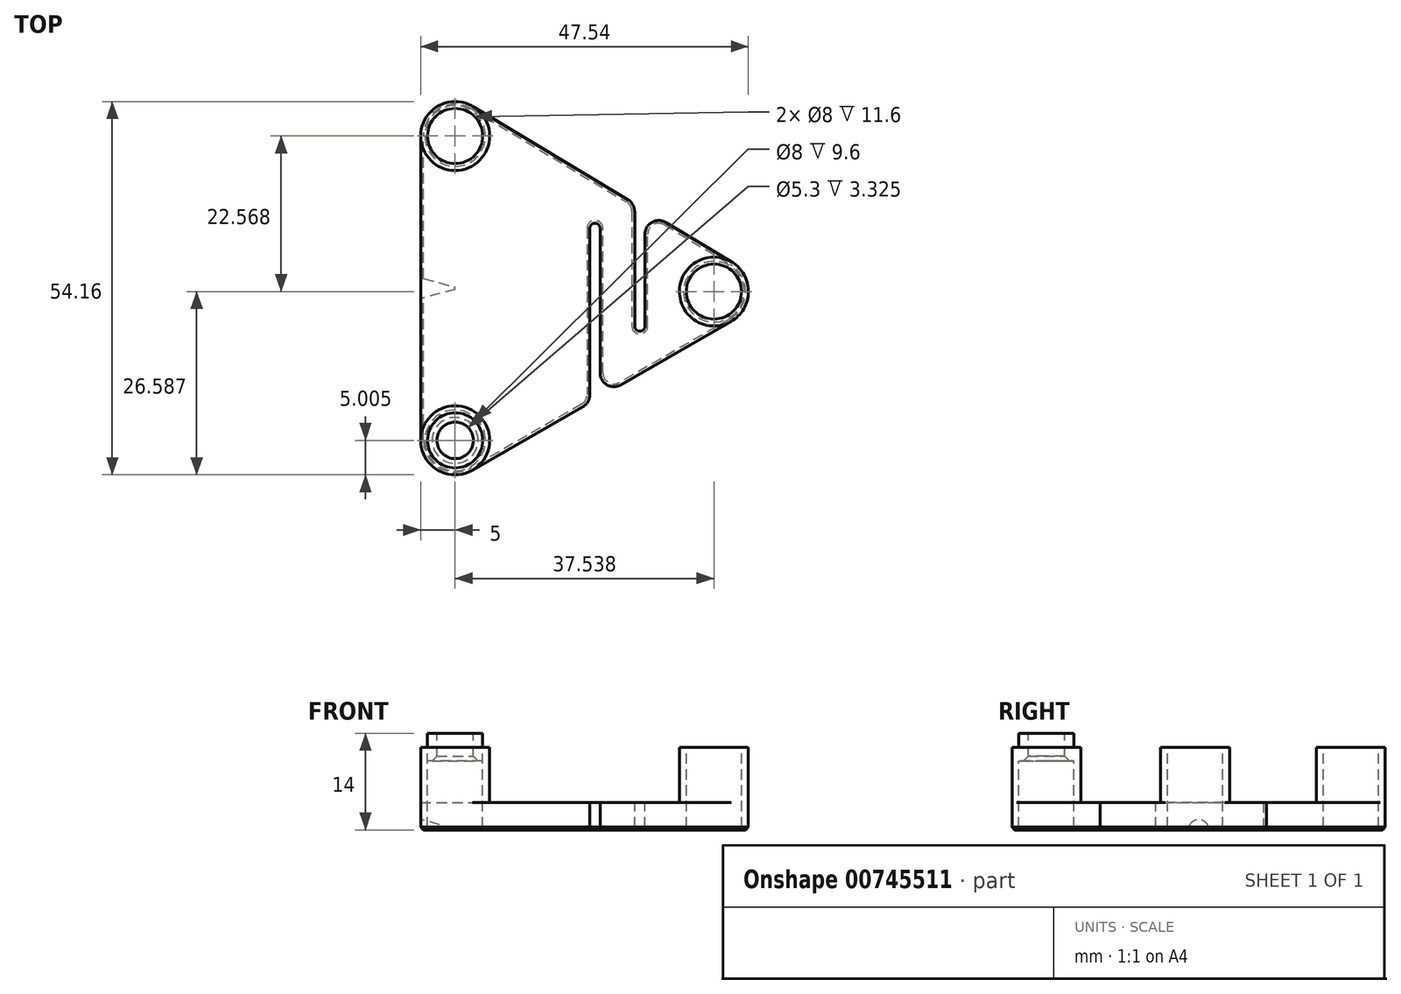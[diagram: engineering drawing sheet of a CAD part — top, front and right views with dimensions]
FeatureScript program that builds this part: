
annotation { "Feature Type Name" : "Feature", "Feature Type Description" : "" }
export const myFeature = defineFeature(function(context is Context, id is Id, definition is map)
    precondition{}
    {
        {
            var Q0;
            Q0=qCreatedBy(makeId("Top.planeOp"),FACE);
            var sketch = newSketch(context, id + "F0", { "sketchPlane" : qUnion([Q0])});
            skLineSegment(sketch, "E0", {"start": v(-11.93, 22.08) * mm, "end": v(25.6, 0.5) * mm, "construction": true});
            skLineSegment(sketch, "E1", {"start": v(25.6, 0.5) * mm, "end": v(-11.93, -22.07) * mm, "construction": true});
            skLineSegment(sketch, "E2", {"start": v(-11.93, -22.07) * mm, "end": v(-11.93, 22.07) * mm, "construction": true});
            skLineSegment(sketch, "E3", {"start": v(0, 0) * mm, "end": v(-11.93, 0) * mm, "construction": true});
            skCircle(sketch, "E4", {"center": v(-11.93, 22.07) * mm, "radius": 2.65 * mm});
            skCircle(sketch, "E5", {"center": v(-11.93, -22.07) * mm, "radius": 2.65 * mm});
            skCircle(sketch, "E6", {"center": v(25.6, 0.5) * mm, "radius": 2.65 * mm});
            skCircle(sketch, "E7", {"center": v(-11.93, 22.07) * mm, "radius": 4 * mm});
            skCircle(sketch, "E8", {"center": v(-11.93, -22.07) * mm, "radius": 4 * mm});
            skCircle(sketch, "E9", {"center": v(25.6, 0.5) * mm, "radius": 4 * mm});
            skLineSegment(sketch, "E10.0", {"start": v(-16.93, -30.92) * mm, "end": v(-16.93, 30.72) * mm});
            skLineSegment(sketch, "E10.1", {"start": v(35.47, 0.59) * mm, "end": v(-16.93, -30.92) * mm});
            skLineSegment(sketch, "E10.2", {"start": v(-16.93, 30.72) * mm, "end": v(35.47, 0.59) * mm});
            skLineSegment(sketch, "E11.top", {"start": v(7.6, -9.43) * mm, "end": v(9.1, -9.43) * mm});
            skLineSegment(sketch, "E11.left", {"start": v(7.6, 16.6) * mm, "end": v(7.6, -9.43) * mm});
            skLineSegment(sketch, "E11.right", {"start": v(9.1, 15.75) * mm, "end": v(9.1, -9.43) * mm});
            skLineSegment(sketch, "E12.bottom", {"start": v(14.1, 6.24) * mm, "end": v(15.6, 6.24) * mm});
            skLineSegment(sketch, "E12.left", {"start": v(14.1, 6.24) * mm, "end": v(14.1, -12.25) * mm});
            skLineSegment(sketch, "E12.right", {"start": v(15.6, 6.24) * mm, "end": v(15.6, -11.35) * mm});
            skCircle(sketch, "E13", {"center": v(-11.93, 22.07) * mm, "radius": 5 * mm});
            skCircle(sketch, "E14", {"center": v(-11.93, -22.07) * mm, "radius": 5 * mm});
            skCircle(sketch, "E15", {"center": v(25.6, 0.5) * mm, "radius": 5 * mm});
            skSolve(sketch);
        }
        {
            var Q0;
            Q0=makeQuery(id+"F0.imprint","IMPRINT",FACE,{"disambiguationData":[TD([[makeQuery(id+"F0.imprint","IMPRINT",EDGE,{"derivedFrom":sQuery(id+"F0.wireOp",EDGE,"E11.top")}),-1.0]])]});
            var Q1;
            Q1=makeQuery(id+"F0.imprint","IMPRINT",FACE,{"disambiguationData":[TD([[makeQuery(id+"F0.imprint","IMPRINT",EDGE,{"derivedFrom":sQuery(id+"F0.wireOp",EDGE,"E7")}),-1.0]])]});
            var Q2;
            Q2=makeQuery(id+"F0.imprint","IMPRINT",FACE,{"disambiguationData":[TD([[makeQuery(id+"F0.imprint","IMPRINT",EDGE,{"derivedFrom":sQuery(id+"F0.wireOp",EDGE,"E8")}),-1.0]])]});
            var Q3;
            Q3=makeQuery(id+"F0.imprint","IMPRINT",FACE,{"disambiguationData":[TD([[makeQuery(id+"F0.imprint","IMPRINT",EDGE,{"derivedFrom":sQuery(id+"F0.wireOp",EDGE,"E9")}),-1.0]])]});
            extrude(context, id + "F1", {"entities" : qUnion([Q0, Q1, Q2, Q3]), "depth" : 4 * mm, "offsetDistance" : 25 * mm});
        }
        {
            var Q0;
            Q0=makeQuery(id+"F1.opExtrude","SWEPT_EDGE",EDGE,{"disambiguationData":[OSD([sQuery(id+"F0.wireOp",EDGE,"E10.0"),sQuery(id+"F0.wireOp",EDGE,"E10.2")])]});
            var Q1;
            Q1=makeQuery(id+"F1.opExtrude","SWEPT_EDGE",EDGE,{"disambiguationData":[OSD([sQuery(id+"F0.wireOp",EDGE,"E10.1"),sQuery(id+"F0.wireOp",EDGE,"E10.2")])]});
            var Q2;
            Q2=makeQuery(id+"F1.opExtrude","SWEPT_EDGE",EDGE,{"disambiguationData":[OSD([sQuery(id+"F0.wireOp",EDGE,"E10.0"),sQuery(id+"F0.wireOp",EDGE,"E10.1")])]});
            fillet(context, id + "F2", {"entities" : qUnion([Q0, Q1, Q2]), "radius" : 2 * mm, "tangentPropagation" : true, "allowEdgeOverflow" : false});
        }
        {
            var Q0;
            Q0=makeQuery(id+"F1.opExtrude","SWEPT_EDGE",EDGE,{"disambiguationData":[OSD([sQuery(id+"F0.wireOp",EDGE,"E11.top"),sQuery(id+"F0.wireOp",EDGE,"E11.left")])]});
            var Q1;
            Q1=makeQuery(id+"F1.opExtrude","SWEPT_EDGE",EDGE,{"disambiguationData":[OSD([sQuery(id+"F0.wireOp",EDGE,"E11.top"),sQuery(id+"F0.wireOp",EDGE,"E11.right")])]});
            var Q2;
            Q2=makeQuery(id+"F1.opExtrude","SWEPT_EDGE",EDGE,{"disambiguationData":[OSD([sQuery(id+"F0.wireOp",EDGE,"E12.bottom"),sQuery(id+"F0.wireOp",EDGE,"E12.left")])]});
            var Q3;
            Q3=makeQuery(id+"F1.opExtrude","SWEPT_EDGE",EDGE,{"disambiguationData":[OSD([sQuery(id+"F0.wireOp",EDGE,"E12.bottom"),sQuery(id+"F0.wireOp",EDGE,"E12.right")])]});
            fillet(context, id + "F3", {"entities" : qUnion([Q0, Q1, Q2, Q3]), "radius" : .75 * mm, "tangentPropagation" : true, "allowEdgeOverflow" : false});
        }
        {
            var Q0;
            Q0=makeQuery(id+"F0.imprint","IMPRINT",FACE,{"disambiguationData":[TD([[makeQuery(id+"F0.imprint","IMPRINT",EDGE,{"derivedFrom":sQuery(id+"F0.wireOp",EDGE,"E7")}),-1.0]])]});
            var Q1;
            Q1=makeQuery(id+"F0.imprint","IMPRINT",FACE,{"disambiguationData":[TD([[makeQuery(id+"F0.imprint","IMPRINT",EDGE,{"derivedFrom":sQuery(id+"F0.wireOp",EDGE,"E8")}),-1.0]])]});
            var Q2;
            Q2=makeQuery(id+"F0.imprint","IMPRINT",FACE,{"disambiguationData":[TD([[makeQuery(id+"F0.imprint","IMPRINT",EDGE,{"derivedFrom":sQuery(id+"F0.wireOp",EDGE,"E9")}),-1.0]])]});
            extrude(context, id + "F4", {"entities" : qUnion([Q0, Q1, Q2]), "operationType" : NewBodyOperationType.ADD, "oppositeDirection" : true, "depth" : 8 * mm, "offsetDistance" : 25 * mm});
        }
        {
            var Q0;
            Q0=makeQuery(id+"F4.opExtrude","CAP_FACE",FACE,{"disambiguationData":[OSD([sQuery(id+"F0.wireOp",EDGE,"E7"),sQuery(id+"F0.wireOp",EDGE,"E13")])],"isStart":false});
            var sketch = newSketch(context, id + "F5", { "sketchPlane" : qUnion([Q0])});
            skCircle(sketch, "E16.0", {"center": v(-11.93, -22.07) * mm, "radius": 4 * mm});
            skCircle(sketch, "E17.0", {"center": v(-11.93, -22.07) * mm, "radius": 2.65 * mm});
            skCircle(sketch, "E18.0", {"center": v(25.6, -0.5) * mm, "radius": 4 * mm});
            skCircle(sketch, "E19.0.0", {"center": v(25.6, -0.5) * mm, "radius": 2.65 * mm});
            skCircle(sketch, "E20.0", {"center": v(-11.93, 22.07) * mm, "radius": 4 * mm});
            skCircle(sketch, "E21.0", {"center": v(-11.93, 22.07) * mm, "radius": 2.65 * mm});
            skSolve(sketch);
        }
        {
            var Q0;
            Q0=makeQuery(id+"F5.imprint","IMPRINT",FACE,{"disambiguationData":[TD([[makeQuery(id+"F5.imprint","IMPRINT",EDGE,{"derivedFrom":sQuery(id+"F5.wireOp",EDGE,"E16.0")}),-1.0]])]});
            var Q1;
            Q1=makeQuery(id+"F5.imprint","IMPRINT",FACE,{"disambiguationData":[TD([[makeQuery(id+"F5.imprint","IMPRINT",EDGE,{"derivedFrom":sQuery(id+"F5.wireOp",EDGE,"E20.0")}),-1.0]])]});
            var Q2;
            Q2=makeQuery(id+"F5.imprint","IMPRINT",FACE,{"disambiguationData":[TD([[makeQuery(id+"F5.imprint","IMPRINT",EDGE,{"derivedFrom":sQuery(id+"F5.wireOp",EDGE,"E18.0")}),-1.0]])]});
            extrude(context, id + "F6", {"entities" : qUnion([Q0, Q1, Q2]), "operationType" : NewBodyOperationType.ADD, "oppositeDirection" : true, "depth" : 2 * mm, "offsetDistance" : 25 * mm, "hasSecondDirection" : true, "secondDirectionOppositeDirection" : false, "secondDirectionDepth" : 2 * mm});
        }
        {
            var Q0;
            Q0=makeQuery(id+"F1.opExtrude","SWEPT_FACE",FACE,{"disambiguationData":[OSD([sQuery(id+"F0.wireOp",EDGE,"E10.0")])]});
            var sketch = newSketch(context, id + "F7", { "sketchPlane" : qUnion([Q0])});
            skCircle(sketch, "E22", {"center": v(0, 4) * mm, "radius": 1.5 * mm});
            skSolve(sketch);
        }
        {
            var Q0;
            Q0=makeQuery(id+"F1.opExtrude","CAP_FACE",FACE,{"disambiguationData":[OSD([sQuery(id+"F0.wireOp",EDGE,"E7"),sQuery(id+"F0.wireOp",EDGE,"E8"),sQuery(id+"F0.wireOp",EDGE,"E9"),sQuery(id+"F0.wireOp",EDGE,"E10.0"),sQuery(id+"F0.wireOp",EDGE,"E10.1"),sQuery(id+"F0.wireOp",EDGE,"E10.2"),sQuery(id+"F0.wireOp",EDGE,"E11.top"),sQuery(id+"F0.wireOp",EDGE,"E11.left"),sQuery(id+"F0.wireOp",EDGE,"E11.right"),sQuery(id+"F0.wireOp",EDGE,"E12.bottom"),sQuery(id+"F0.wireOp",EDGE,"E12.left"),sQuery(id+"F0.wireOp",EDGE,"E12.right"),sQuery(id+"F0.wireOp",EDGE,"E13"),sQuery(id+"F0.wireOp",EDGE,"E14"),sQuery(id+"F0.wireOp",EDGE,"E15")])],"isStart":false});
            chamfer(context, id + "F8", {"entities" : qUnion([Q0]), "width" : .4 * mm, "tangentPropagation" : true});
        }
        {
            var Q0;
            {var subQ0=sQuery(id+"F7.wireOp",EDGE,"E22");var subQ1=makeQuery(id+"F1.opExtrude","CAP_EDGE",EDGE,{"disambiguationData":[OSD([sQuery(id+"F0.wireOp",EDGE,"E10.0")])],"isStart":false});var subQ2=makeQuery(id+"F7.imprint","INTERSECT",VERTEX,{"disambiguationData":[OD(0.0)],"derivedFrom":[subQ1,subQ0]});Q0=makeQuery(id+"F7.imprint","IMPRINT",FACE,{"disambiguationData":[TD([[makeQuery(id+"F7.imprint","IMPRINT",EDGE,{"disambiguationData":[TD([[subQ2,1.0]])],"derivedFrom":subQ0}),1.0]])]});}
            var Q1;
            {var subQ0=sQuery(id+"F7.wireOp",EDGE,"E22");var subQ1=makeQuery(id+"F1.opExtrude","CAP_EDGE",EDGE,{"disambiguationData":[OSD([sQuery(id+"F0.wireOp",EDGE,"E10.0")])],"isStart":false});var subQ2=makeQuery(id+"F7.imprint","INTERSECT",VERTEX,{"disambiguationData":[OD(0.0)],"derivedFrom":[subQ1,subQ0]});Q1=makeQuery(id+"F7.imprint","IMPRINT",FACE,{"disambiguationData":[TD([[makeQuery(id+"F7.imprint","IMPRINT",EDGE,{"disambiguationData":[TD([[subQ2,-1.0]])],"derivedFrom":subQ0}),1.0]])]});}
            extrude(context, id + "F9", {"entities" : qUnion([Q0, Q1]), "operationType" : NewBodyOperationType.REMOVE, "oppositeDirection" : true, "depth" : 5 * mm, "offsetDistance" : 25 * mm, "hasDraft" : true, "draftAngle" : 15 * degree, "draftPullDirection" : true});
        }
        {
            var Q0;
            Q0=makeQuery(id+"F6.opExtrude","CAP_EDGE",EDGE,{"disambiguationData":[OSD([sQuery(id+"F5.wireOp",EDGE,"E16.0")])],"isStart":false});
            var Q1;
            Q1=makeQuery(id+"F6.opExtrude","CAP_EDGE",EDGE,{"disambiguationData":[OSD([sQuery(id+"F5.wireOp",EDGE,"E18.0")])],"isStart":false});
            var Q2;
            Q2=makeQuery(id+"F6.opExtrude","CAP_EDGE",EDGE,{"disambiguationData":[OSD([sQuery(id+"F5.wireOp",EDGE,"E17.0")])],"isStart":false});
            var Q3;
            Q3=makeQuery(id+"F6.opExtrude","CAP_EDGE",EDGE,{"disambiguationData":[OSD([sQuery(id+"F5.wireOp",EDGE,"E19.0.0")])],"isStart":false});
            var Q4;
            Q4=makeQuery(id+"F6.opExtrude","CAP_EDGE",EDGE,{"disambiguationData":[OSD([sQuery(id+"F5.wireOp",EDGE,"E21.0")])],"isStart":false});
            var Q5;
            Q5=makeQuery(id+"F6.opExtrude","CAP_EDGE",EDGE,{"disambiguationData":[OSD([sQuery(id+"F5.wireOp",EDGE,"E20.0")])],"isStart":false});
            chamfer(context, id + "F10", {"entities" : qUnion([Q0, Q1, Q2, Q3, Q4, Q5]), "width" : (1.35 / 2) * mm, "tangentPropagation" : true});
        }
        {
            var Q0;
            Q0=makeQuery(id+"F1.opExtrude","SWEPT_BODY",BODY,{"disambiguationData":[OSD([sQuery(id+"F0.wireOp",EDGE,"E7"),sQuery(id+"F0.wireOp",EDGE,"E8"),sQuery(id+"F0.wireOp",EDGE,"E9"),sQuery(id+"F0.wireOp",EDGE,"E10.0"),sQuery(id+"F0.wireOp",EDGE,"E10.1"),sQuery(id+"F0.wireOp",EDGE,"E10.2"),sQuery(id+"F0.wireOp",EDGE,"E11.top"),sQuery(id+"F0.wireOp",EDGE,"E11.left"),sQuery(id+"F0.wireOp",EDGE,"E11.right"),sQuery(id+"F0.wireOp",EDGE,"E12.bottom"),sQuery(id+"F0.wireOp",EDGE,"E12.left"),sQuery(id+"F0.wireOp",EDGE,"E12.right"),sQuery(id+"F0.wireOp",EDGE,"E13"),sQuery(id+"F0.wireOp",EDGE,"E14"),sQuery(id+"F0.wireOp",EDGE,"E15")])]});
            var Q1;
            Q1=sQuery(id+"F0.wireOp",EDGE,"E3");
            transform(context, id + "F11", {"entities" : qUnion([Q0]), "transformType" : TransformType.ROTATION, "transformAxis" : qUnion([Q1]), "angle" : 180 * degree, "makeCopy" : false});
        }
    });
